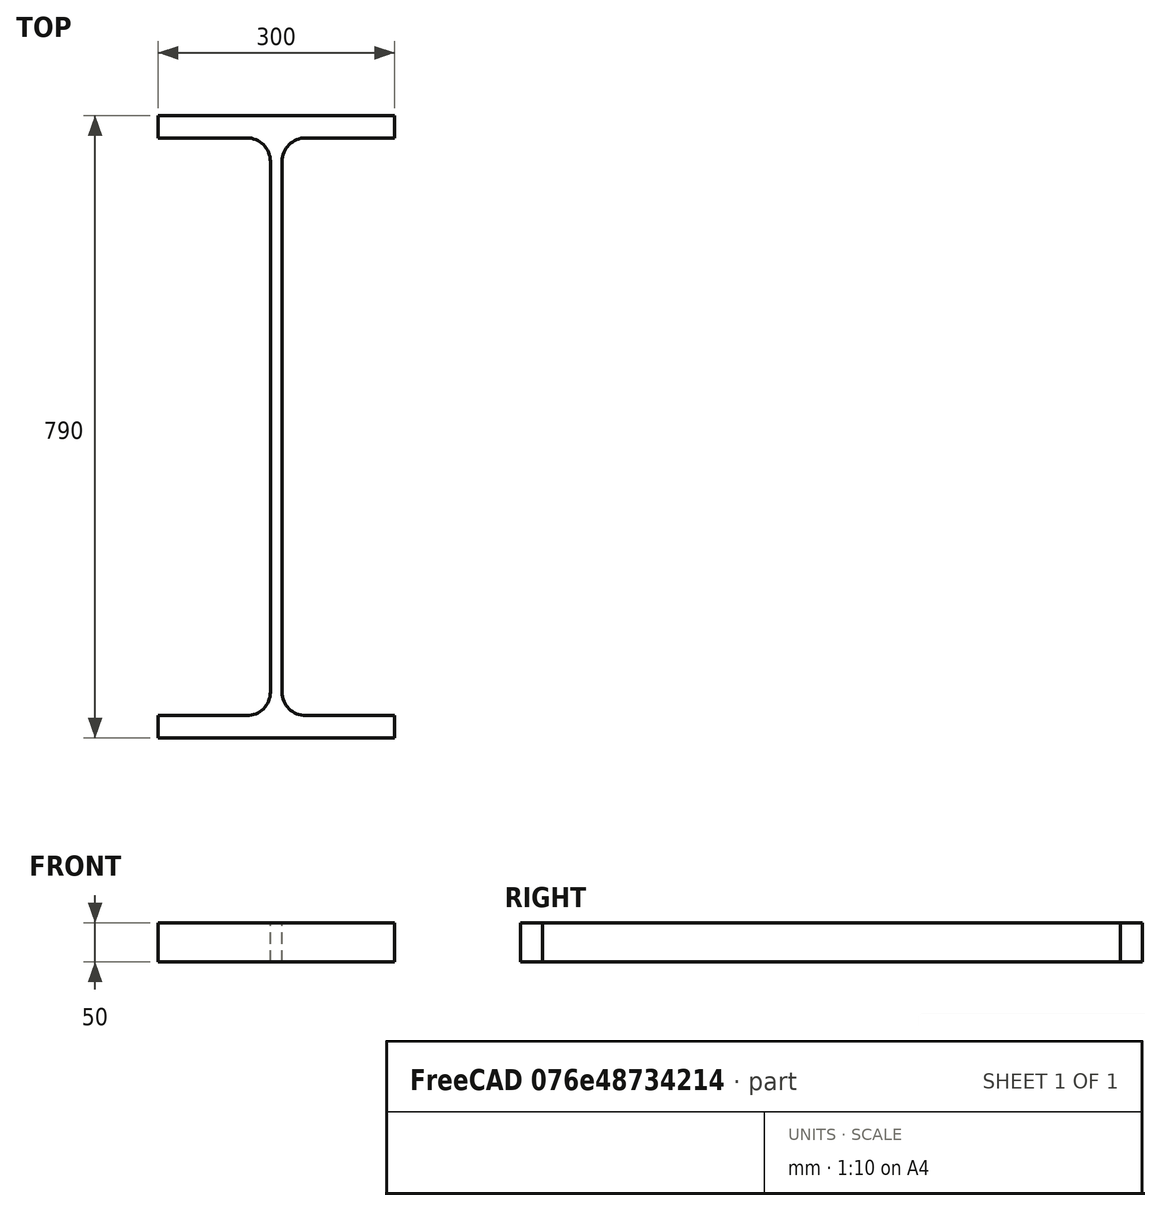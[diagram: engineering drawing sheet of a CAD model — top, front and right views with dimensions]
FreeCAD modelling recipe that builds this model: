
FCSTD DOCUMENT  (FreeCAD 0.15R4671 (Git))
Label: HE-A-Profile 800 DIN1025-3 S235JR
License: All rights reserved
LicenseURL: http://en.wikipedia.org/wiki/All_rights_reserved
objects: Sketcher::SketchObject×1, Part::Extrusion×1
note: 2 computed .brp shape members not serialized (recipe doc carries the construction recipe); baked Part::Feature solids carry a one-line shape summary decoded from their .brp

FEATURE [Sketcher::SketchObject] Sketch
  sketch-geometry (16):
    g0: LineSegment StartX=7.5 StartY=-337 StartZ=0 EndX=7.5 EndY=337 EndZ=0
    g1: LineSegment StartX=37.5 StartY=367 StartZ=0 EndX=150 EndY=367 EndZ=0
    g2: LineSegment StartX=150 StartY=367 StartZ=0 EndX=150 EndY=395 EndZ=0
    g3: LineSegment StartX=150 StartY=395 StartZ=0 EndX=-150 EndY=395 EndZ=0
    g4: LineSegment StartX=-150 StartY=395 StartZ=0 EndX=-150 EndY=367 EndZ=0
    g5: LineSegment StartX=-150 StartY=367 StartZ=0 EndX=-37.5 EndY=367 EndZ=0
    g6: LineSegment StartX=-7.5 StartY=337 StartZ=0 EndX=-7.5 EndY=-337 EndZ=0
    g7: LineSegment StartX=-37.5 StartY=-367 StartZ=0 EndX=-150 EndY=-367 EndZ=0
    g8: LineSegment StartX=-150 StartY=-367 StartZ=0 EndX=-150 EndY=-395 EndZ=0
    g9: LineSegment StartX=-150 StartY=-395 StartZ=0 EndX=150 EndY=-395 EndZ=0
    g10: LineSegment StartX=150 StartY=-395 StartZ=0 EndX=150 EndY=-367 EndZ=0
    g11: LineSegment StartX=150 StartY=-367 StartZ=0 EndX=37.5 EndY=-367 EndZ=0
    g12: ArcOfCircle CenterX=37.5 CenterY=337 CenterZ=0 NormalX=0 NormalY=0 NormalZ=1 Radius=30 StartAngle=1.5708 EndAngle=3.14159
    g13: ArcOfCircle CenterX=37.5 CenterY=-337 CenterZ=0 NormalX=0 NormalY=0 NormalZ=1 Radius=30 StartAngle=3.14159 EndAngle=4.71239
    g14: ArcOfCircle CenterX=-37.5 CenterY=337 CenterZ=0 NormalX=0 NormalY=0 NormalZ=1 Radius=30 StartAngle=0 EndAngle=1.5708
    g15: ArcOfCircle CenterX=-37.5 CenterY=-337 CenterZ=0 NormalX=0 NormalY=0 NormalZ=1 Radius=30 StartAngle=4.71239 EndAngle=6.28319
  constraints (42):
    c: Vertical(g0)
    c: Coincident(g2,g1)
    c: Vertical(g2)
    c: Coincident(g3,g2)
    c: Coincident(g4,g3)
    c: Vertical(g4)
    c: Coincident(g5,g4)
    c: Horizontal(g5)
    c: Vertical(g6)
    c: Horizontal(g7)
    c: Coincident(g8,g7)
    c: Vertical(g8)
    c: Coincident(g9,g8)
    c: Horizontal(g9)
    c: Coincident(g10,g9)
    c: Vertical(g10)
    c: Coincident(g11,g10)
    c: Horizontal(g11)
    c: Tangent(g1,g12) = 1.5708
    c: Tangent(g0,g12) = 1.5708
    c: Tangent(g0,g13) = 1.5708
    c: Tangent(g11,g13) = 1.5708
    c: Tangent(g5,g14) = 1.5708
    c: Tangent(g6,g14) = 1.5708
    c: Tangent(g6,g15) = 1.5708
    c: Tangent(g7,g15) = 1.5708
    c: Equal(g3,g9)
    c: Equal(g2,g4)
    c: Equal(g4,g8)
    c: Equal(g8,g10)
    c: Equal(g12,g14)
    c: Equal(g14,g15)
    c: Equal(g15,g13)
    c: Symmetric(g2,g3,g-2)
    c: Symmetric(g9,g8,g-2)
    c: Symmetric(g0,g6,g-2)
    c: Symmetric(g2,g9,g-1)
    c: DistanceY(g2,g9) = -790
    c: DistanceX(g3) = -300
    c: DistanceX(g0,g6) = -15
    c: DistanceY(g2) = 28
    c: Radius(g12) = 30
FEATURE [Part::Extrusion] Extrude  label="HE-A-Profile 800 DIN1025-3 S235JR"
  Base = -> Sketch
  Dir = (0,0,50)
  Solid = true
